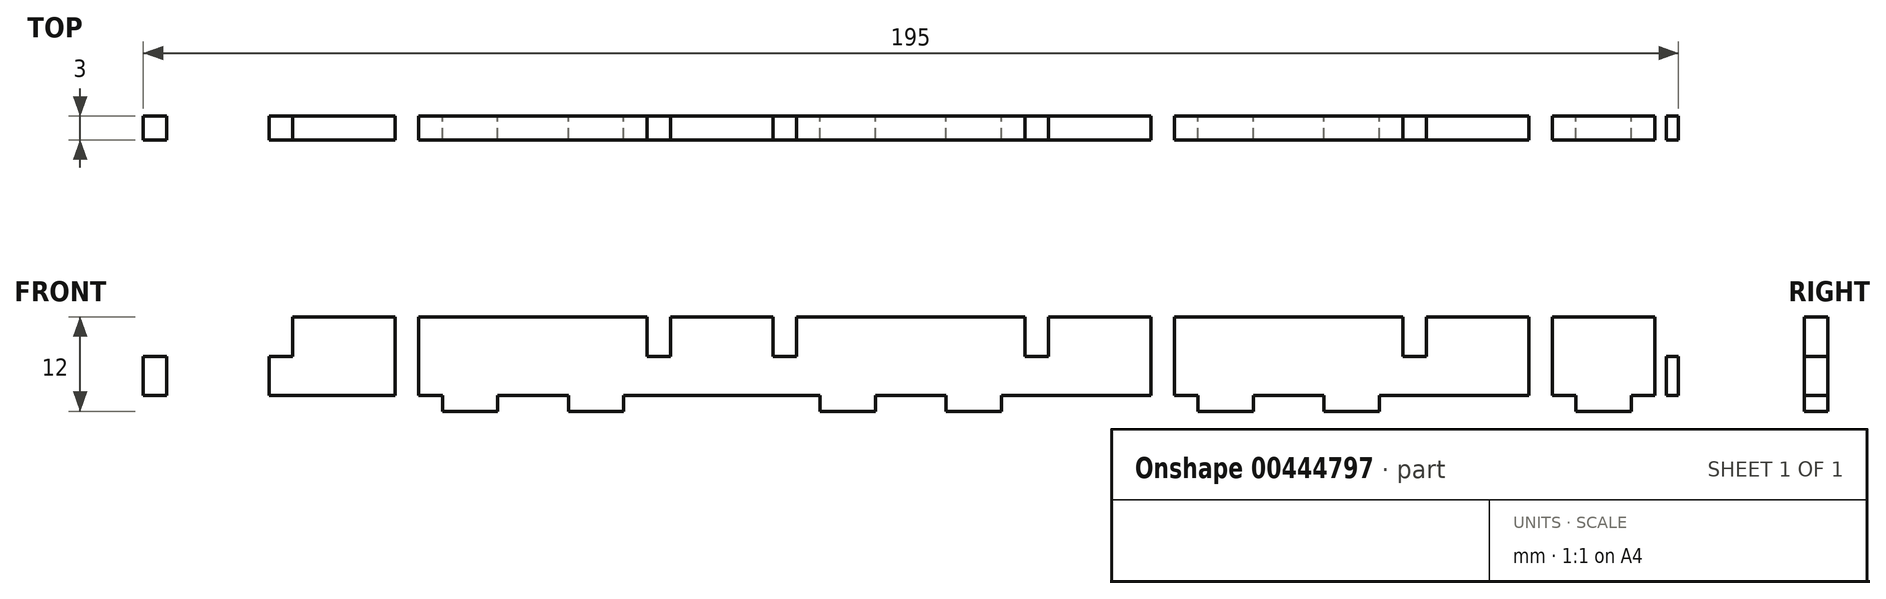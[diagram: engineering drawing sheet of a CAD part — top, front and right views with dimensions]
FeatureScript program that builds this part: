
annotation { "Feature Type Name" : "Feature", "Feature Type Description" : "" }
export const myFeature = defineFeature(function(context is Context, id is Id, definition is map)
    precondition{}
    {
        {
            var Q0;
            Q0=qCreatedBy(makeId("Front.planeOp"),FACE);
            var sketch = newSketch(context, id + "F0", { "sketchPlane" : qUnion([Q0])});
            skLineSegment(sketch, "E0", {"start": v(0, 0) * mm, "end": v(4.5, 0) * mm});
            skLineSegment(sketch, "E1", {"start": v(4.5, 0) * mm, "end": v(4.5, -2) * mm});
            skLineSegment(sketch, "E2", {"start": v(4.5, -2) * mm, "end": v(11.5, -2) * mm});
            skLineSegment(sketch, "E3", {"start": v(11.5, -2) * mm, "end": v(11.5, 0) * mm});
            skLineSegment(sketch, "E4", {"start": v(11.5, 0) * mm, "end": v(36.5, 0) * mm});
            skLineSegment(sketch, "E5", {"start": v(36.5, 0) * mm, "end": v(36.5, -2) * mm});
            skLineSegment(sketch, "E6", {"start": v(36.5, -2) * mm, "end": v(43.5, -2) * mm});
            skLineSegment(sketch, "E7", {"start": v(43.5, -2) * mm, "end": v(43.5, 0) * mm});
            skLineSegment(sketch, "E8", {"start": v(43.5, 0) * mm, "end": v(48, 0) * mm});
            skLineSegment(sketch, "E9.1.0.0", {"start": v(52.5, -2) * mm, "end": v(59.5, -2) * mm});
            skLineSegment(sketch, "E9.1.0.1", {"start": v(59.5, 0) * mm, "end": v(84.5, 0) * mm});
            skLineSegment(sketch, "E9.1.0.2", {"start": v(84.5, -2) * mm, "end": v(91.5, -2) * mm});
            skLineSegment(sketch, "E9.1.0.3", {"start": v(91.5, 0) * mm, "end": v(96, 0) * mm});
            skLineSegment(sketch, "E9.1.0.4", {"start": v(48, 0) * mm, "end": v(52.5, 0) * mm});
            skLineSegment(sketch, "E9.1.0.5", {"start": v(52.5, 0) * mm, "end": v(52.5, -2) * mm});
            skLineSegment(sketch, "E9.1.0.6", {"start": v(91.5, -2) * mm, "end": v(91.5, 0) * mm});
            skLineSegment(sketch, "E9.1.0.7", {"start": v(59.5, -2) * mm, "end": v(59.5, 0) * mm});
            skLineSegment(sketch, "E9.1.0.8", {"start": v(84.5, 0) * mm, "end": v(84.5, -2) * mm});
            skLineSegment(sketch, "E9.2.0.0", {"start": v(100.5, -2) * mm, "end": v(107.5, -2) * mm});
            skLineSegment(sketch, "E9.2.0.1", {"start": v(107.5, 0) * mm, "end": v(132.5, 0) * mm});
            skLineSegment(sketch, "E9.2.0.2", {"start": v(132.5, -2) * mm, "end": v(139.5, -2) * mm});
            skLineSegment(sketch, "E9.2.0.3", {"start": v(139.5, 0) * mm, "end": v(144, 0) * mm});
            skLineSegment(sketch, "E9.2.0.4", {"start": v(96, 0) * mm, "end": v(100.5, 0) * mm});
            skLineSegment(sketch, "E9.2.0.5", {"start": v(100.5, 0) * mm, "end": v(100.5, -2) * mm});
            skLineSegment(sketch, "E9.2.0.6", {"start": v(139.5, -2) * mm, "end": v(139.5, 0) * mm});
            skLineSegment(sketch, "E9.2.0.7", {"start": v(107.5, -2) * mm, "end": v(107.5, 0) * mm});
            skLineSegment(sketch, "E9.2.0.8", {"start": v(132.5, 0) * mm, "end": v(132.5, -2) * mm});
            skLineSegment(sketch, "E9.3.0.0", {"start": v(148.5, -2) * mm, "end": v(155.5, -2) * mm});
            skLineSegment(sketch, "E9.3.0.1", {"start": v(155.5, 0) * mm, "end": v(180.5, 0) * mm});
            skLineSegment(sketch, "E9.3.0.2", {"start": v(180.5, -2) * mm, "end": v(187.5, -2) * mm});
            skLineSegment(sketch, "E9.3.0.3", {"start": v(187.5, 0) * mm, "end": v(192, 0) * mm});
            skLineSegment(sketch, "E9.3.0.4", {"start": v(144, 0) * mm, "end": v(148.5, 0) * mm});
            skLineSegment(sketch, "E9.3.0.5", {"start": v(148.5, 0) * mm, "end": v(148.5, -2) * mm});
            skLineSegment(sketch, "E9.3.0.6", {"start": v(187.5, -2) * mm, "end": v(187.5, 0) * mm});
            skLineSegment(sketch, "E9.3.0.7", {"start": v(155.5, -2) * mm, "end": v(155.5, 0) * mm});
            skLineSegment(sketch, "E9.3.0.8", {"start": v(180.5, 0) * mm, "end": v(180.5, -2) * mm});
            skLineSegment(sketch, "E9.direction1", {"start": v(0, 0) * mm, "end": v(48, 0) * mm, "construction": true});
            skLineSegment(sketch, "E10", {"start": v(0, 0) * mm, "end": v(0, 10) * mm});
            skLineSegment(sketch, "E11", {"start": v(192, 0) * mm, "end": v(192, 10) * mm});
            skLineSegment(sketch, "E12", {"start": v(192, 10) * mm, "end": v(0, 10) * mm});
            skPoint(sketch, "E13.oppositeSnap0", {"position": v(0, 5) * mm});
            skLineSegment(sketch, "E13.bottom", {"start": v(0, 10) * mm, "end": v(-1.5, 10) * mm});
            skLineSegment(sketch, "E13.top", {"start": v(0, 5) * mm, "end": v(-1.5, 5) * mm});
            skLineSegment(sketch, "E13.left", {"start": v(0, 10) * mm, "end": v(0, 5) * mm});
            skLineSegment(sketch, "E13.right", {"start": v(-1.5, 10) * mm, "end": v(-1.5, 5) * mm});
            skPoint(sketch, "E14.oppositeSnap0", {"position": v(192, 5) * mm});
            skLineSegment(sketch, "E14.bottom", {"start": v(192, 10) * mm, "end": v(193.5, 10) * mm});
            skLineSegment(sketch, "E14.top", {"start": v(192, 5) * mm, "end": v(193.5, 5) * mm});
            skLineSegment(sketch, "E14.left", {"start": v(192, 10) * mm, "end": v(192, 5) * mm});
            skLineSegment(sketch, "E14.right", {"start": v(193.5, 10) * mm, "end": v(193.5, 5) * mm});
            skLineSegment(sketch, "E15.bottom", {"start": v(14.5, 10) * mm, "end": v(17.5, 10) * mm});
            skLineSegment(sketch, "E15.top", {"start": v(14.5, 5) * mm, "end": v(17.5, 5) * mm});
            skLineSegment(sketch, "E15.left", {"start": v(14.5, 10) * mm, "end": v(14.5, 5) * mm});
            skLineSegment(sketch, "E15.right", {"start": v(17.5, 10) * mm, "end": v(17.5, 5) * mm});
            skLineSegment(sketch, "E16.bottom", {"start": v(33.5, 10) * mm, "end": v(30.5, 10) * mm});
            skLineSegment(sketch, "E16.top", {"start": v(33.5, 5) * mm, "end": v(30.5, 5) * mm});
            skLineSegment(sketch, "E16.left", {"start": v(33.5, 10) * mm, "end": v(33.5, 5) * mm});
            skLineSegment(sketch, "E16.right", {"start": v(30.5, 10) * mm, "end": v(30.5, 5) * mm});
            skLineSegment(sketch, "E17.bottom", {"start": v(62.5, 10) * mm, "end": v(65.5, 10) * mm});
            skLineSegment(sketch, "E17.top", {"start": v(62.5, 5) * mm, "end": v(65.5, 5) * mm});
            skLineSegment(sketch, "E17.left", {"start": v(62.5, 10) * mm, "end": v(62.5, 5) * mm});
            skLineSegment(sketch, "E17.right", {"start": v(65.5, 10) * mm, "end": v(65.5, 5) * mm});
            skLineSegment(sketch, "E18.bottom", {"start": v(78.5, 10) * mm, "end": v(81.5, 10) * mm});
            skLineSegment(sketch, "E18.top", {"start": v(78.5, 5) * mm, "end": v(81.5, 5) * mm});
            skLineSegment(sketch, "E18.left", {"start": v(78.5, 10) * mm, "end": v(78.5, 5) * mm});
            skLineSegment(sketch, "E18.right", {"start": v(81.5, 10) * mm, "end": v(81.5, 5) * mm});
            skLineSegment(sketch, "E19.bottom", {"start": v(110.5, 10) * mm, "end": v(113.5, 10) * mm});
            skLineSegment(sketch, "E19.top", {"start": v(110.5, 5) * mm, "end": v(113.5, 5) * mm});
            skLineSegment(sketch, "E19.left", {"start": v(110.5, 10) * mm, "end": v(110.5, 5) * mm});
            skLineSegment(sketch, "E19.right", {"start": v(113.5, 10) * mm, "end": v(113.5, 5) * mm});
            skLineSegment(sketch, "E20.bottom", {"start": v(129.5, 10) * mm, "end": v(126.5, 10) * mm});
            skLineSegment(sketch, "E20.top", {"start": v(129.5, 5) * mm, "end": v(126.5, 5) * mm});
            skLineSegment(sketch, "E20.left", {"start": v(129.5, 10) * mm, "end": v(129.5, 5) * mm});
            skLineSegment(sketch, "E20.right", {"start": v(126.5, 10) * mm, "end": v(126.5, 5) * mm});
            skLineSegment(sketch, "E21.bottom", {"start": v(158.5, 10) * mm, "end": v(161.5, 10) * mm});
            skLineSegment(sketch, "E21.top", {"start": v(158.5, 5) * mm, "end": v(161.5, 5) * mm});
            skLineSegment(sketch, "E21.left", {"start": v(158.5, 10) * mm, "end": v(158.5, 5) * mm});
            skLineSegment(sketch, "E21.right", {"start": v(161.5, 10) * mm, "end": v(161.5, 5) * mm});
            skLineSegment(sketch, "E22.bottom", {"start": v(177.5, 10) * mm, "end": v(174.5, 10) * mm});
            skLineSegment(sketch, "E22.top", {"start": v(177.5, 5) * mm, "end": v(174.5, 5) * mm});
            skLineSegment(sketch, "E22.left", {"start": v(177.5, 10) * mm, "end": v(177.5, 5) * mm});
            skLineSegment(sketch, "E22.right", {"start": v(174.5, 10) * mm, "end": v(174.5, 5) * mm});
            skLineSegment(sketch, "E23.top", {"start": v(0, 0) * mm, "end": v(-1.5, 0) * mm});
            skLineSegment(sketch, "E23.left", {"start": v(0, 5) * mm, "end": v(0, 0) * mm});
            skLineSegment(sketch, "E23.right", {"start": v(-1.5, 5) * mm, "end": v(-1.5, 0) * mm});
            skLineSegment(sketch, "E24.top", {"start": v(14.5, 0) * mm, "end": v(17.5, 0) * mm});
            skLineSegment(sketch, "E24.left", {"start": v(14.5, 5) * mm, "end": v(14.5, 0) * mm});
            skLineSegment(sketch, "E24.right", {"start": v(17.5, 5) * mm, "end": v(17.5, 0) * mm});
            skLineSegment(sketch, "E25.bottom", {"start": v(30.5, 5) * mm, "end": v(33.5, 5) * mm});
            skLineSegment(sketch, "E25.top", {"start": v(30.5, 0) * mm, "end": v(33.5, 0) * mm});
            skLineSegment(sketch, "E25.left", {"start": v(30.5, 5) * mm, "end": v(30.5, 0) * mm});
            skLineSegment(sketch, "E25.right", {"start": v(33.5, 5) * mm, "end": v(33.5, 0) * mm});
            skLineSegment(sketch, "E26.top", {"start": v(62.5, 0) * mm, "end": v(65.5, 0) * mm});
            skLineSegment(sketch, "E26.left", {"start": v(62.5, 5) * mm, "end": v(62.5, 0) * mm});
            skLineSegment(sketch, "E26.right", {"start": v(65.5, 5) * mm, "end": v(65.5, 0) * mm});
            skLineSegment(sketch, "E27.top", {"start": v(78.5, 0) * mm, "end": v(81.5, 0) * mm});
            skLineSegment(sketch, "E27.left", {"start": v(78.5, 5) * mm, "end": v(78.5, 0) * mm});
            skLineSegment(sketch, "E27.right", {"start": v(81.5, 5) * mm, "end": v(81.5, 0) * mm});
            skLineSegment(sketch, "E28.top", {"start": v(110.5, 0) * mm, "end": v(113.5, 0) * mm});
            skLineSegment(sketch, "E28.left", {"start": v(110.5, 5) * mm, "end": v(110.5, 0) * mm});
            skLineSegment(sketch, "E28.right", {"start": v(113.5, 5) * mm, "end": v(113.5, 0) * mm});
            skLineSegment(sketch, "E29.bottom", {"start": v(126.5, 5) * mm, "end": v(129.5, 5) * mm});
            skLineSegment(sketch, "E29.top", {"start": v(126.5, 0) * mm, "end": v(129.5, 0) * mm});
            skLineSegment(sketch, "E29.left", {"start": v(126.5, 5) * mm, "end": v(126.5, 0) * mm});
            skLineSegment(sketch, "E29.right", {"start": v(129.5, 5) * mm, "end": v(129.5, 0) * mm});
            skLineSegment(sketch, "E30.top", {"start": v(158.5, 0) * mm, "end": v(161.5, 0) * mm});
            skLineSegment(sketch, "E30.left", {"start": v(158.5, 5) * mm, "end": v(158.5, 0) * mm});
            skLineSegment(sketch, "E30.right", {"start": v(161.5, 5) * mm, "end": v(161.5, 0) * mm});
            skLineSegment(sketch, "E31.bottom", {"start": v(174.5, 5) * mm, "end": v(177.5, 5) * mm});
            skLineSegment(sketch, "E31.top", {"start": v(174.5, 0) * mm, "end": v(177.5, 0) * mm});
            skLineSegment(sketch, "E31.left", {"start": v(174.5, 5) * mm, "end": v(174.5, 0) * mm});
            skLineSegment(sketch, "E31.right", {"start": v(177.5, 5) * mm, "end": v(177.5, 0) * mm});
            skLineSegment(sketch, "E32.top", {"start": v(192, 0) * mm, "end": v(193.5, 0) * mm});
            skLineSegment(sketch, "E32.left", {"start": v(192, 5) * mm, "end": v(192, 0) * mm});
            skLineSegment(sketch, "E32.right", {"start": v(193.5, 5) * mm, "end": v(193.5, 0) * mm});
            skLineSegment(sketch, "E33.bottom", {"start": v(0, 10) * mm, "end": v(1.5, 10) * mm});
            skLineSegment(sketch, "E33.top", {"start": v(0, 5) * mm, "end": v(1.5, 5) * mm});
            skLineSegment(sketch, "E33.right", {"start": v(1.5, 10) * mm, "end": v(1.5, 5) * mm});
            skLineSegment(sketch, "E34.bottom", {"start": v(1.5, 5) * mm, "end": v(0, 5) * mm});
            skLineSegment(sketch, "E34.top", {"start": v(1.5, 0) * mm, "end": v(0, 0) * mm});
            skLineSegment(sketch, "E34.left", {"start": v(1.5, 5) * mm, "end": v(1.5, 0) * mm});
            skLineSegment(sketch, "E35.bottom", {"start": v(192, 10) * mm, "end": v(190.5, 10) * mm});
            skLineSegment(sketch, "E35.top", {"start": v(192, 5) * mm, "end": v(190.5, 5) * mm});
            skLineSegment(sketch, "E35.right", {"start": v(190.5, 10) * mm, "end": v(190.5, 5) * mm});
            skLineSegment(sketch, "E36.bottom", {"start": v(190.5, 5) * mm, "end": v(192, 5) * mm});
            skLineSegment(sketch, "E36.top", {"start": v(190.5, 0) * mm, "end": v(192, 0) * mm});
            skLineSegment(sketch, "E36.left", {"start": v(190.5, 5) * mm, "end": v(190.5, 0) * mm});
            skLineSegment(sketch, "E37.bottom", {"start": v(14.5, 10) * mm, "end": v(11.5, 10) * mm});
            skLineSegment(sketch, "E37.top", {"start": v(14.5, 13) * mm, "end": v(11.5, 13) * mm});
            skLineSegment(sketch, "E37.left", {"start": v(14.5, 10) * mm, "end": v(14.5, 13) * mm});
            skLineSegment(sketch, "E37.right", {"start": v(11.5, 10) * mm, "end": v(11.5, 13) * mm});
            skLineSegment(sketch, "E38.bottom", {"start": v(17.5, 10) * mm, "end": v(20.5, 10) * mm});
            skLineSegment(sketch, "E38.top", {"start": v(17.5, 13) * mm, "end": v(20.5, 13) * mm});
            skLineSegment(sketch, "E38.left", {"start": v(17.5, 10) * mm, "end": v(17.5, 13) * mm});
            skLineSegment(sketch, "E38.right", {"start": v(20.5, 10) * mm, "end": v(20.5, 13) * mm});
            skLineSegment(sketch, "E39.bottom", {"start": v(177.5, 10) * mm, "end": v(180.5, 10) * mm});
            skLineSegment(sketch, "E39.top", {"start": v(177.5, 13) * mm, "end": v(180.5, 13) * mm});
            skLineSegment(sketch, "E39.left", {"start": v(177.5, 10) * mm, "end": v(177.5, 13) * mm});
            skLineSegment(sketch, "E39.right", {"start": v(180.5, 10) * mm, "end": v(180.5, 13) * mm});
            skLineSegment(sketch, "E40.bottom", {"start": v(174.5, 10) * mm, "end": v(171.5, 10) * mm});
            skLineSegment(sketch, "E40.top", {"start": v(174.5, 13) * mm, "end": v(171.5, 13) * mm});
            skLineSegment(sketch, "E40.left", {"start": v(174.5, 10) * mm, "end": v(174.5, 13) * mm});
            skLineSegment(sketch, "E40.right", {"start": v(171.5, 10) * mm, "end": v(171.5, 13) * mm});
            skSolve(sketch);
        }
        {
            var Q0;
            Q0=makeQuery(id+"F0.imprint","IMPRINT",FACE,{"disambiguationData":[TD([[makeQuery(id+"F0.imprint","IMPRINT",EDGE,{"derivedFrom":sQuery(id+"F0.wireOp",EDGE,"E0")}),1.0]])]});
            var Q1;
            Q1=makeQuery(id+"F0.imprint","IMPRINT",FACE,{"disambiguationData":[TD([[makeQuery(id+"F0.imprint","IMPRINT",EDGE,{"derivedFrom":sQuery(id+"F0.wireOp",EDGE,"E15.top")}),-1.0]])]});
            var Q2;
            {var subQ1=sQuery(id+"F0.wireOp",EDGE,"E15.right");Q2=makeQuery(id+"F0.imprint","IMPRINT",FACE,{"disambiguationData":[TD([[makeQuery(id+"F0.imprint","IMPRINT",EDGE,{"derivedFrom":subQ1}),1.0]])]});}
            var Q3;
            Q3=makeQuery(id+"F0.imprint","IMPRINT",FACE,{"disambiguationData":[TD([[makeQuery(id+"F0.imprint","IMPRINT",EDGE,{"derivedFrom":sQuery(id+"F0.wireOp",EDGE,"E25.bottom")}),-1.0]])]});
            var Q4;
            {var subQ4=sQuery(id+"F0.wireOp",EDGE,"E5");Q4=makeQuery(id+"F0.imprint","IMPRINT",FACE,{"disambiguationData":[TD([[makeQuery(id+"F0.imprint","IMPRINT",EDGE,{"derivedFrom":subQ4}),1.0]])]});}
            var Q5;
            Q5=makeQuery(id+"F0.imprint","IMPRINT",FACE,{"disambiguationData":[TD([[makeQuery(id+"F0.imprint","IMPRINT",EDGE,{"derivedFrom":sQuery(id+"F0.wireOp",EDGE,"E17.top")}),-1.0]])]});
            var Q6;
            {var subQ0=sQuery(id+"F0.wireOp",EDGE,"E17.right");Q6=makeQuery(id+"F0.imprint","IMPRINT",FACE,{"disambiguationData":[TD([[makeQuery(id+"F0.imprint","IMPRINT",EDGE,{"derivedFrom":subQ0}),1.0]])]});}
            var Q7;
            Q7=makeQuery(id+"F0.imprint","IMPRINT",FACE,{"disambiguationData":[TD([[makeQuery(id+"F0.imprint","IMPRINT",EDGE,{"derivedFrom":sQuery(id+"F0.wireOp",EDGE,"E18.top")}),-1.0]])]});
            var Q8;
            Q8=makeQuery(id+"F0.imprint","IMPRINT",FACE,{"disambiguationData":[TD([[makeQuery(id+"F0.imprint","IMPRINT",EDGE,{"derivedFrom":sQuery(id+"F0.wireOp",EDGE,"E9.1.0.2")}),1.0]])]});
            var Q9;
            Q9=makeQuery(id+"F0.imprint","IMPRINT",FACE,{"disambiguationData":[TD([[makeQuery(id+"F0.imprint","IMPRINT",EDGE,{"derivedFrom":sQuery(id+"F0.wireOp",EDGE,"E19.top")}),-1.0]])]});
            var Q10;
            {var subQ2=sQuery(id+"F0.wireOp",EDGE,"E19.right");Q10=makeQuery(id+"F0.imprint","IMPRINT",FACE,{"disambiguationData":[TD([[makeQuery(id+"F0.imprint","IMPRINT",EDGE,{"derivedFrom":subQ2}),1.0]])]});}
            var Q11;
            Q11=makeQuery(id+"F0.imprint","IMPRINT",FACE,{"disambiguationData":[TD([[makeQuery(id+"F0.imprint","IMPRINT",EDGE,{"derivedFrom":sQuery(id+"F0.wireOp",EDGE,"E29.bottom")}),-1.0]])]});
            var Q12;
            Q12=makeQuery(id+"F0.imprint","IMPRINT",FACE,{"disambiguationData":[TD([[makeQuery(id+"F0.imprint","IMPRINT",EDGE,{"derivedFrom":sQuery(id+"F0.wireOp",EDGE,"E9.2.0.2")}),1.0]])]});
            var Q13;
            Q13=makeQuery(id+"F0.imprint","IMPRINT",FACE,{"disambiguationData":[TD([[makeQuery(id+"F0.imprint","IMPRINT",EDGE,{"derivedFrom":sQuery(id+"F0.wireOp",EDGE,"E21.top")}),-1.0]])]});
            var Q14;
            {var subQ1=sQuery(id+"F0.wireOp",EDGE,"E21.right");Q14=makeQuery(id+"F0.imprint","IMPRINT",FACE,{"disambiguationData":[TD([[makeQuery(id+"F0.imprint","IMPRINT",EDGE,{"derivedFrom":subQ1}),1.0]])]});}
            var Q15;
            Q15=makeQuery(id+"F0.imprint","IMPRINT",FACE,{"disambiguationData":[TD([[makeQuery(id+"F0.imprint","IMPRINT",EDGE,{"derivedFrom":sQuery(id+"F0.wireOp",EDGE,"E31.bottom")}),-1.0]])]});
            var Q16;
            Q16=makeQuery(id+"F0.imprint","IMPRINT",FACE,{"disambiguationData":[TD([[makeQuery(id+"F0.imprint","IMPRINT",EDGE,{"derivedFrom":sQuery(id+"F0.wireOp",EDGE,"E9.3.0.2")}),1.0]])]});
            var Q17;
            Q17=makeQuery(id+"F0.imprint","IMPRINT",FACE,{"disambiguationData":[TD([[makeQuery(id+"F0.imprint","IMPRINT",EDGE,{"derivedFrom":sQuery(id+"F0.wireOp",EDGE,"E34.bottom")}),1.0]])]});
            var Q18;
            Q18=makeQuery(id+"F0.imprint","IMPRINT",FACE,{"disambiguationData":[TD([[makeQuery(id+"F0.imprint","IMPRINT",EDGE,{"derivedFrom":sQuery(id+"F0.wireOp",EDGE,"E36.bottom")}),-1.0]])]});
            var Q19;
            Q19=makeQuery(id+"F0.imprint","IMPRINT",FACE,{"disambiguationData":[TD([[makeQuery(id+"F0.imprint","IMPRINT",EDGE,{"derivedFrom":sQuery(id+"F0.wireOp",EDGE,"E14.top")}),-1.0]])]});
            var Q20;
            Q20=makeQuery(id+"F0.imprint","IMPRINT",FACE,{"disambiguationData":[TD([[makeQuery(id+"F0.imprint","IMPRINT",EDGE,{"derivedFrom":sQuery(id+"F0.wireOp",EDGE,"E13.top")}),1.0]])]});
            var Q21;
            Q21=makeQuery(id+"F0.imprint","IMPRINT",FACE,{"disambiguationData":[TD([[makeQuery(id+"F0.imprint","IMPRINT",EDGE,{"derivedFrom":sQuery(id+"F0.wireOp",EDGE,"E40.bottom")}),-1.0]])]});
            var Q22;
            Q22=makeQuery(id+"F0.imprint","IMPRINT",FACE,{"disambiguationData":[TD([[makeQuery(id+"F0.imprint","IMPRINT",EDGE,{"derivedFrom":sQuery(id+"F0.wireOp",EDGE,"E39.bottom")}),1.0]])]});
            var Q23;
            Q23=makeQuery(id+"F0.imprint","IMPRINT",FACE,{"disambiguationData":[TD([[makeQuery(id+"F0.imprint","IMPRINT",EDGE,{"derivedFrom":sQuery(id+"F0.wireOp",EDGE,"E38.bottom")}),1.0]])]});
            var Q24;
            Q24=makeQuery(id+"F0.imprint","IMPRINT",FACE,{"disambiguationData":[TD([[makeQuery(id+"F0.imprint","IMPRINT",EDGE,{"derivedFrom":sQuery(id+"F0.wireOp",EDGE,"E37.bottom")}),-1.0]])]});
            extrude(context, id + "F1", {"entities" : qUnion([Q0, Q1, Q2, Q3, Q4, Q5, Q6, Q7, Q8, Q9, Q10, Q11, Q12, Q13, Q14, Q15, Q16, Q17, Q18, Q19, Q20, Q21, Q22, Q23, Q24]), "depth" : 3 * mm});
        }
    });
